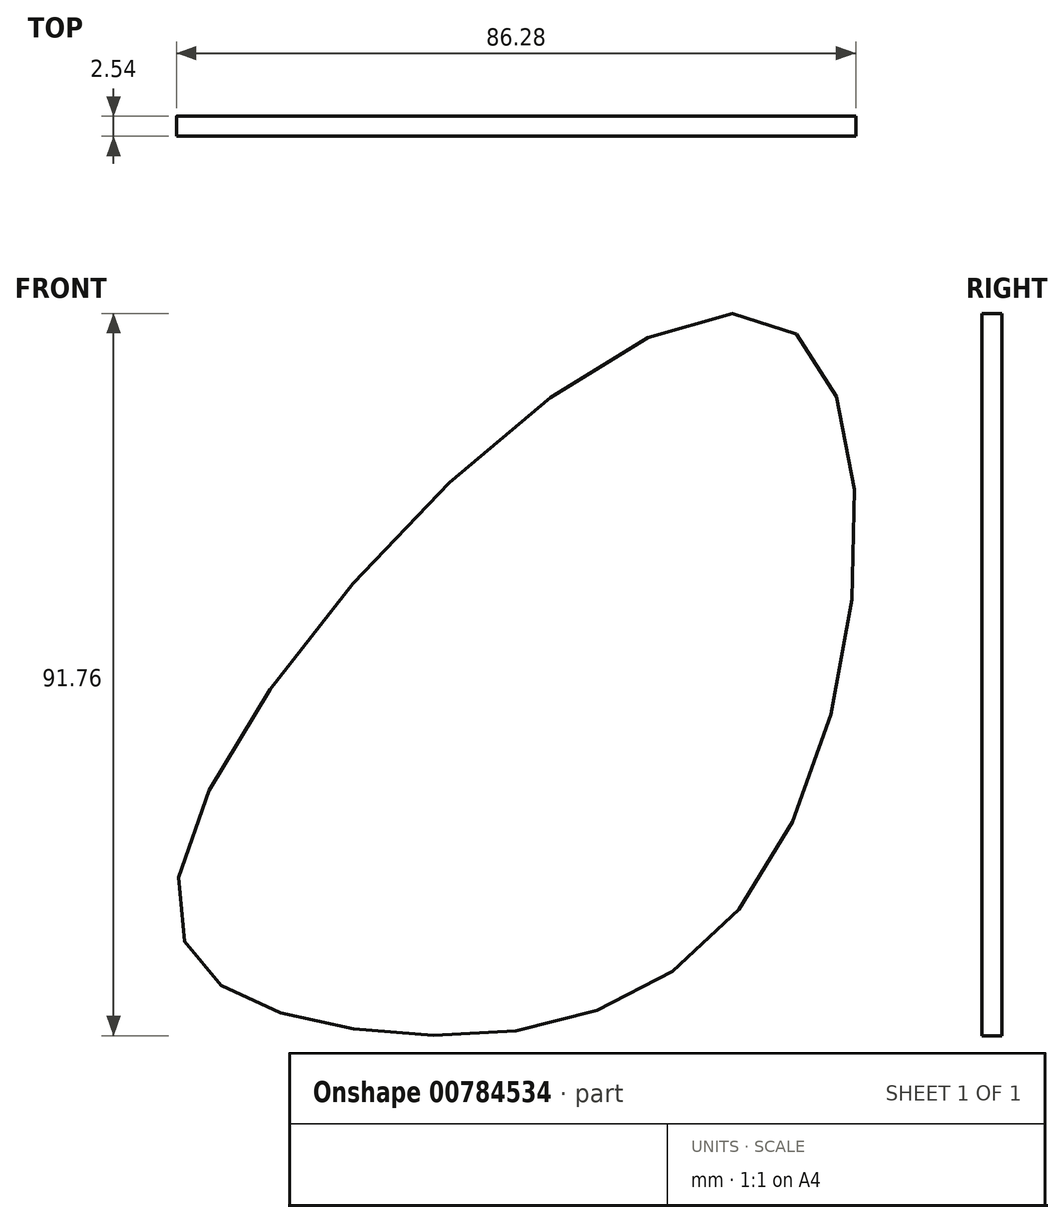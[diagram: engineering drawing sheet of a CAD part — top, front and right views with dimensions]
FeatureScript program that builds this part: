
annotation { "Feature Type Name" : "Feature", "Feature Type Description" : "" }
export const myFeature = defineFeature(function(context is Context, id is Id, definition is map)
    precondition{}
    {
        {
            var Q0;
            Q0=qCreatedBy(makeId("Front.planeOp"),FACE);
            var sketch = newSketch(context, id + "F0", { "sketchPlane" : qUnion([Q0])});
            skFitSpline(sketch, "E0", {"points": [v(0, 0) * mm, v(74.14, 71.27) * mm, v(74.14, 0) * mm, v(21.55, -19.15) * mm, v(0, 0) * mm]});
            skSolve(sketch);
        }
        {
            var Q0;
            Q0 = qSketchRegion(id + "F0", true);
            extrude(context, id + "F1", {"entities" : qUnion([Q0]), "depth" : 2.54 * mm, "offsetDistance" : 25.4 * mm});
        }
    });
